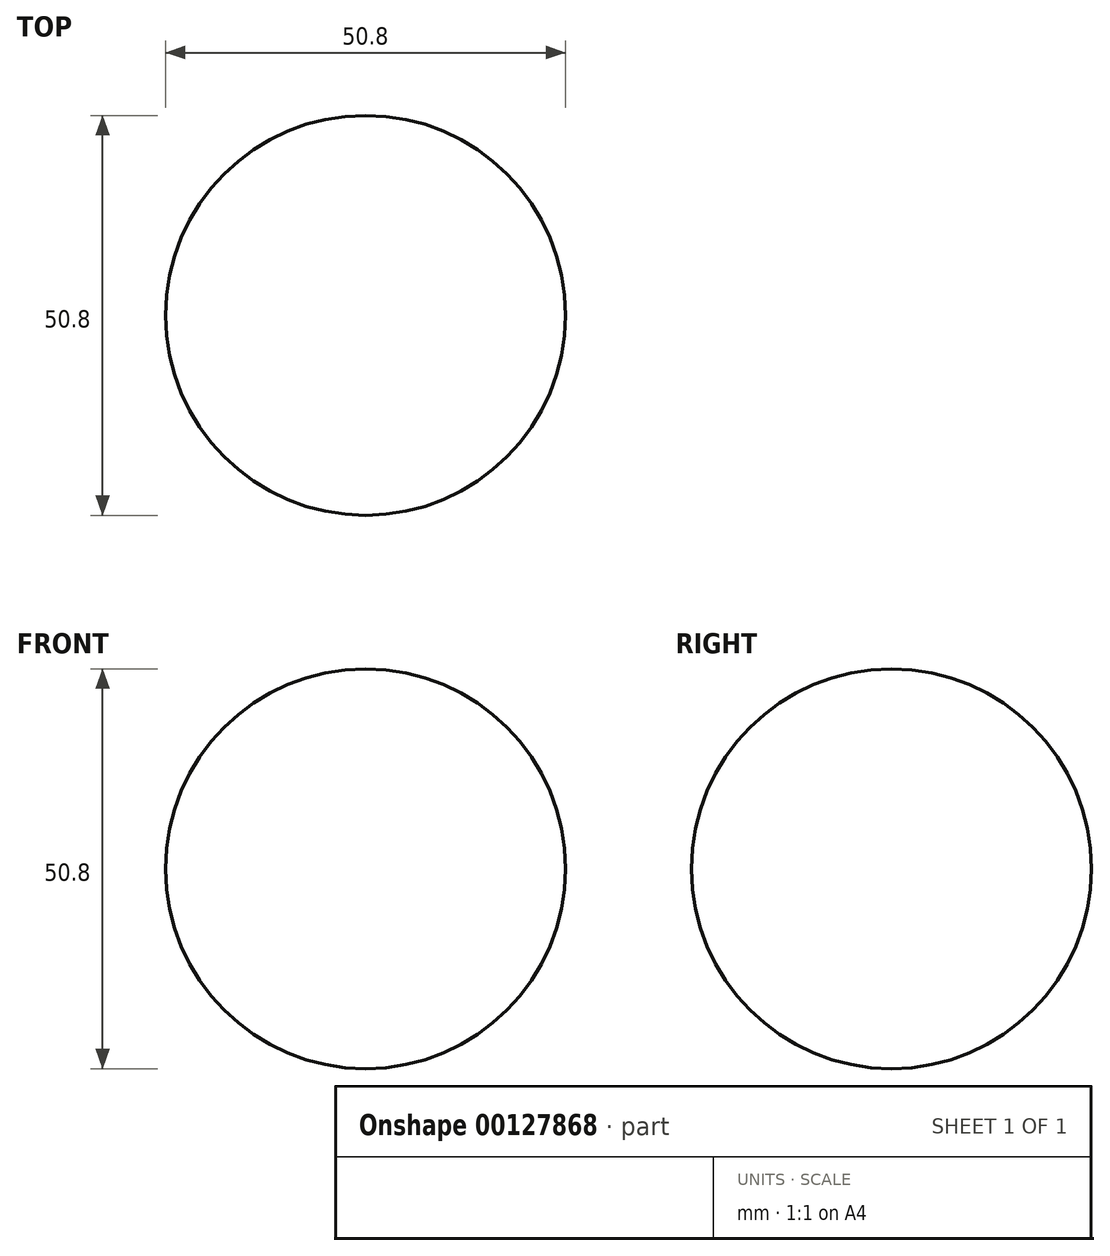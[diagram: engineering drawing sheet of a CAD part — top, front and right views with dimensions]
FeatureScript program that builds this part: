
annotation { "Feature Type Name" : "Feature", "Feature Type Description" : "" }
export const myFeature = defineFeature(function(context is Context, id is Id, definition is map)
    precondition{}
    {
        {
            var Q0;
            Q0=qCreatedBy(makeId("Top.planeOp"),FACE);
            var sketch = newSketch(context, id + "F0", { "sketchPlane" : qUnion([Q0])});
            skArc(sketch, "E0", {"start": v(-25.4, 0) * mm, "mid": v(0, 25.4) * mm, "end": v(25.4, 0) * mm});
            skLineSegment(sketch, "E1", {"start": v(0, 0) * mm, "end": v(123.09, 0) * mm});
            skSolve(sketch);
        }
        {
            var Q0;
            Q0=sQuery(id+"F0.wireOp",EDGE,"E0");
            var Q1;
            Q1=sQuery(id+"F0.wireOp",EDGE,"E1");
            revolve(context, id + "F1", {"bodyType" : ToolBodyType.SURFACE, "surfaceEntities" : qUnion([Q0]), "axis" : qUnion([Q1]), "revolveType" : RevolveType.FULL});
        }
    });
